# Revit family: Evoflat WSS_RFA_1
name_source: partatom
category: Mechanical Equipment
units: mm (PartAtom-declared; Revit-internal decimal feet)

## family parameters
Always vertical = Yes
Classification = None
Cut with Voids When Loaded = No
OmniClass Number = 23.75.65.11.11
OmniClass Title = Heating Controllers
Part Type = Normal
Room Calculation Point = No
Round Connector Dimension = Use Diameter
Shared = No
Work Plane-Based = No

## types (6) — shared parameters
Connection = G 3/4 Internal Thread
D = 20 mm  [stored 0.0656168 ft]
Description = Flat Station
Front Insulation = Yes
H = 588 mm
H1 = 5 mm  [stored 0.0164042 ft]
H2 = 13 mm
H3 = 575 mm  [stored 1.88648 ft]
IfcExportAs = IfcFlowController
IfcExportType = EvoFlat WSS
Insulation Material = Danfoss EPP insulation
L = 545 mm  [stored 1.78806 ft]
L1 = 112 mm  [stored 0.367454 ft]
L1a = 43 mm  [stored 0.141076 ft]
LOD 200 = No
LOD 350 = Yes
Manufacturer = Danfoss
Nominal Pressure = PN 10
Nut size = 30 mm
Type Image = <None>
Voltage = 230 V
W = 150 mm
W1 = 44 mm  [stored 0.144357 ft]
Weight = 8.50 kg
With Front Insulation = Yes

## per-type parameters (varying)
| type | DHW Flow Rate Primary | DHW Pressure Loss Primary | DHW Tap Load 50°C | DHW Temperature DHS/DHR | DHW capacity | HEX material | Model | Model Type |
| Evoflat WSS_Type 1_Cu_Ins_145G0190 | 850 l/h | 40 kPa | 15.3 l/min | 65/22 °C | 43 kW | Danfoss Copper | 145G0190 | Evoflat WSS_Type 1_Cu_Ins |
| Evoflat WSS_Type 2_Cu_Ins_145G0191 | 950 l/h | 30 kPa | 17.5 l/min | 65/21 °C | 49 kW | Danfoss Copper | 145G0191 | Evoflat WSS_Type 2_Cu_Ins |
| Evoflat WSS_Type 3_Cu_Ins_145G0192 | 950 l/h | 27 kPa | 19.4 l/min | 65/16 °C | 55 kW | Danfoss Copper | 145G0192 | Evoflat WSS_Type 3_Cu_Ins |
| Evoflat WSS_Type 1_StS_Ins_145G0219 | 850 l/h | 40 kPa | 15.3 l/min | 65/22 °C | 43 kW | Danfoss Stainless Steel | 145G0219 | Evoflat WSS_Type 1_StS_Ins |
| Evoflat WSS_Type 2_StS_Ins_145G0220 | 950 l/h | 30 kPa | 17.5 l/min | 65/21 °C | 49 kW | Danfoss Stainless Steel | 145G0220 | Evoflat WSS_Type 2_StS_Ins |
| Evoflat WSS_Type 3_StS_Ins_145G0221 | 950 l/h | 27 kPa | 19.4 l/min | 65/16 °C | 55 kW | Danfoss Stainless Steel | 145G0221 | Evoflat WSS_Type 3_StS_Ins |

note: [stored X ft] marks values corroborated as IEEE doubles in the binary element streams (Revit-internal decimal feet)

## geometry (parser evidence)
native form markers: Sweep x2
no freeform markers — native parametric forms only
